# Revit family: 265-91-001 DN250-300
name_source: partatom
category: Pipe Accessories
units: mm (PartAtom-declared; Revit-internal decimal feet)

## family parameters
Always vertical = Yes
Cut with Voids When Loaded = No
Part Type = Valve - Breaks Into
Round Connector Dimension = Use Diameter
Shared = No
Work Plane-Based = No

## types (4) — shared parameters
25 = 25 mm  [stored 0.082021 ft]
Bolt.no = 12 mm  [stored 0.0393701 ft]
DN250_PN10 = 265-9-0250-10-14036400
DN250_PN16 = 265-9-0250-11-04036401
DN300_PN10 = 265-9-0300-10-14036400
DN300_PN16 = 265-9-0300-11-04036401
Description_ = AVK DISMANTLING JOINT WITH CENTRE FLANGE, PN10/16
Search_table = 265-91-001 DN250-300
T = 7 mm  [stored 0.0229659 ft]
URL_product_pages = https://www.avkvalves.com
zero-valued in all types: Default Elevation

## per-type parameters (varying)
| type | B1 | Bore | D | DN | FL_T | FL_T/2 | L | L1 | L11 | L2 | L3 | Nut_T | PCD | PN | Raised_dis | S | S11 | T1 | offset | raised_R |
| DN250_PN16 | 30 mm  [stored 0.0984252 ft] | 125 mm  [stored 0.410105 ft] | 200 mm  [stored 0.656168 ft] | 250 mm  [stored 0.82021 ft] | 22 mm  [stored 0.0721785 ft] | 11 mm  [stored 0.0360892 ft] | 380 mm | 156 mm | 230 mm  [stored 0.754593 ft] | 25 mm  [stored 0.082021 ft] | 11 mm  [stored 0.0360892 ft] | 17 mm | 178 mm | 16 mm  [stored 0.0524934 ft] | 3 mm  [stored 0.00984252 ft] | 24 mm  [stored 0.0787402 ft] | 32 mm  [stored 0.104987 ft] | 17 mm | 8 mm  [stored 0.0262467 ft] | 150 mm  [stored 0.492126 ft] |
| DN250_PN10 | 29 mm | 125 mm  [stored 0.410105 ft] | 203 mm | 250 mm  [stored 0.82021 ft] | 22 mm  [stored 0.0721785 ft] | 11 mm  [stored 0.0360892 ft] | 360 mm  [stored 1.1811 ft] | 150 mm  [stored 0.492126 ft] | 220 mm  [stored 0.721785 ft] | 23 mm | 11 mm  [stored 0.0360892 ft] | 17 mm | 175 mm  [stored 0.574147 ft] | 10 mm  [stored 0.0328084 ft] | 3 mm  [stored 0.00984252 ft] | 20 mm  [stored 0.0656168 ft] | 27 mm  [stored 0.0885827 ft] | 17 mm | 7 mm  [stored 0.0229659 ft] | 152 mm |
| DN300_PN10 | 29 mm | 150 mm  [stored 0.492126 ft] | 228 mm | 300 mm  [stored 0.984252 ft] | 25 mm  [stored 0.082021 ft] | 12 mm  [stored 0.0393701 ft] | 360 mm  [stored 1.1811 ft] | 150 mm  [stored 0.492126 ft] | 220 mm  [stored 0.721785 ft] | 23 mm | 12 mm  [stored 0.0393701 ft] | 18 mm | 200 mm  [stored 0.656168 ft] | 10 mm  [stored 0.0328084 ft] | 4 mm  [stored 0.0131234 ft] | 20 mm  [stored 0.0656168 ft] | 27 mm  [stored 0.0885827 ft] | 18 mm | 7 mm  [stored 0.0229659 ft] | 171 mm |
| DN300_PN16 | 32 mm  [stored 0.104987 ft] | 150 mm  [stored 0.492126 ft] | 228 mm | 300 mm  [stored 0.984252 ft] | 25 mm  [stored 0.082021 ft] | 12 mm  [stored 0.0393701 ft] | 405 mm | 170 mm  [stored 0.557743 ft] | 250 mm  [stored 0.82021 ft] | 26 mm | 12 mm  [stored 0.0393701 ft] | 18 mm | 205 mm  [stored 0.672572 ft] | 16 mm  [stored 0.0524934 ft] | 4 mm  [stored 0.0131234 ft] | 24 mm  [stored 0.0787402 ft] | 32 mm  [stored 0.104987 ft] | 18 mm | 8 mm  [stored 0.0262467 ft] | 171 mm |

note: [stored X ft] marks values corroborated as IEEE doubles in the binary element streams (Revit-internal decimal feet)

## geometry (parser evidence)
native form markers: Sweep x10
no freeform markers — native parametric forms only
